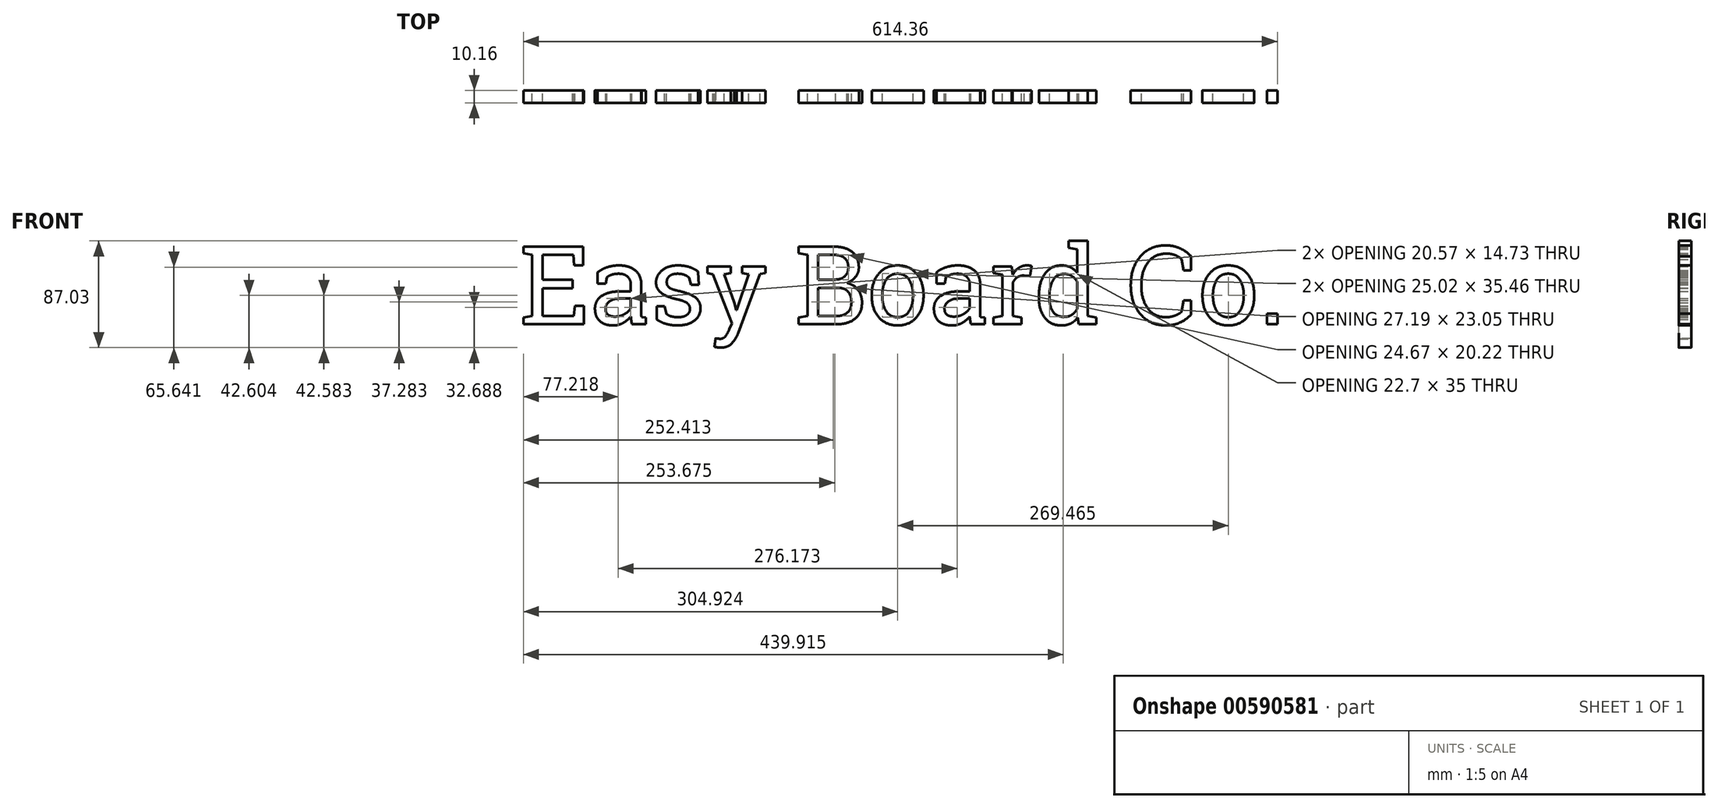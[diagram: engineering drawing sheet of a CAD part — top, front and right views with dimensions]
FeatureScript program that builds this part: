
annotation { "Feature Type Name" : "Feature", "Feature Type Description" : "" }
export const myFeature = defineFeature(function(context is Context, id is Id, definition is map)
    precondition{}
    {
        {
            var Q0;
            Q0=qCreatedBy(makeId("Front.planeOp"),FACE);
            var sketch = newSketch(context, id + "F0", { "sketchPlane" : qUnion([Q0])});
            skText(sketch, "E0", { "text": "Easy Board Co.", "fontName": "RobotoSlab-Regular.ttf"});
            const initialGuessF0  = {"E0": [-0.33864, -0.0281, 1, 0, 0.06426]};
            skSetInitialGuess(sketch, initialGuessF0);
            skSolve(sketch);
        }
        {
            var Q0;
            Q0 = qSketchRegion(id + "F0", true);
            extrude(context, id + "F1", {"entities" : qUnion([Q0]), "depth" : 10.16 * mm, "offsetDistance" : 25.4 * mm});
        }
    });
